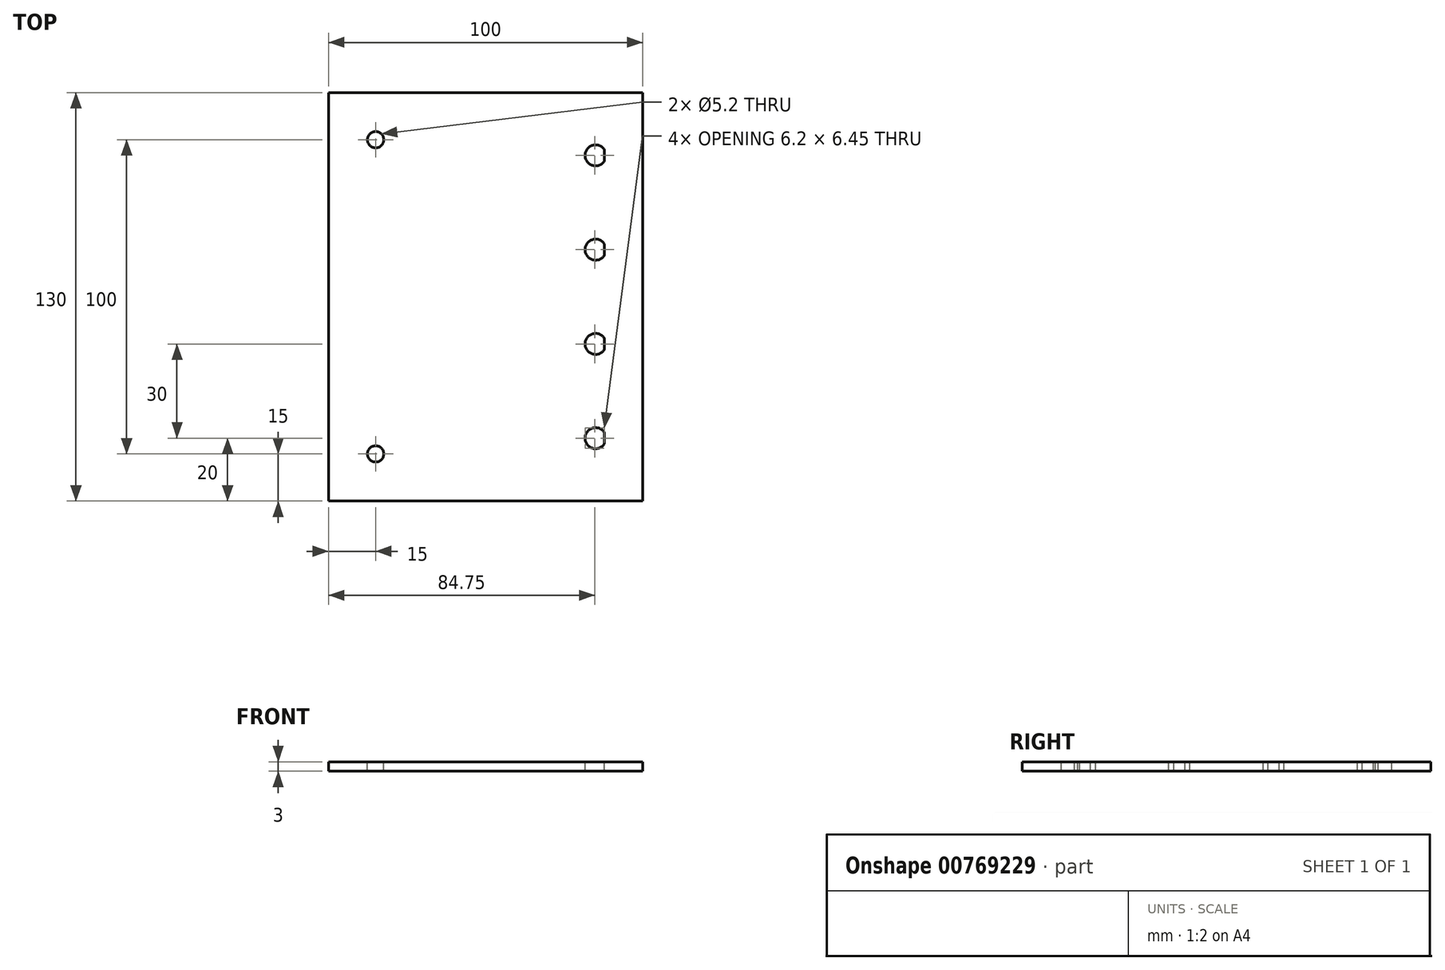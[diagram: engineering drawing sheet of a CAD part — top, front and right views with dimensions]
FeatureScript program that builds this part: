
annotation { "Feature Type Name" : "Feature", "Feature Type Description" : "" }
export const myFeature = defineFeature(function(context is Context, id is Id, definition is map)
    precondition{}
    {
        {
            var Q0;
            Q0=qCreatedBy(makeId("Top.planeOp"),FACE);
            var sketch = newSketch(context, id + "F0", { "sketchPlane" : qUnion([Q0])});
            skLineSegment(sketch, "E0.bottom", {"start": v(-56.25, -56.34) * mm, "end": v(43.75, -56.34) * mm});
            skLineSegment(sketch, "E0.top", {"start": v(-56.25, 73.66) * mm, "end": v(43.75, 73.66) * mm});
            skLineSegment(sketch, "E0.left", {"start": v(-56.25, -56.34) * mm, "end": v(-56.25, 73.66) * mm});
            skLineSegment(sketch, "E0.right", {"start": v(43.75, -56.34) * mm, "end": v(43.75, 73.66) * mm});
            skSolve(sketch);
        }
        {
            var Q0;
            Q0 = qSketchRegion(id + "F0", true);
            extrude(context, id + "F1", {"entities" : qUnion([Q0]), "depth" : 3 * mm, "offsetDistance" : 25 * mm});
        }
        {
            var Q0;
            Q0=makeQuery(id+"F1.opExtrude","CAP_FACE",FACE,{"disambiguationData":[OSD([sQuery(id+"F0.wireOp",EDGE,"E0.bottom"),sQuery(id+"F0.wireOp",EDGE,"E0.top"),sQuery(id+"F0.wireOp",EDGE,"E0.left"),sQuery(id+"F0.wireOp",EDGE,"E0.right")])],"isStart":false});
            var sketch = newSketch(context, id + "F2", { "sketchPlane" : qUnion([Q0])});
            skPoint(sketch, "E1", {"position": v(-41.25, -41.34) * mm});
            skPoint(sketch, "E2", {"position": v(-41.25, 58.66) * mm});
            skCircle(sketch, "E3", {"center": v(-41.25, -41.34) * mm, "radius": 2.6 * mm});
            skCircle(sketch, "E4", {"center": v(-41.25, 58.66) * mm, "radius": 2.6 * mm});
            skSolve(sketch);
        }
        {
            var Q0;
            Q0 = qSketchRegion(id + "F2", true);
            extrude(context, id + "F3", {"entities" : qUnion([Q0]), "operationType" : NewBodyOperationType.REMOVE, "endBound" : BoundingType.THROUGH_ALL, "oppositeDirection" : true, "depth" : 25 * mm, "offsetDistance" : 25 * mm});
        }
        {
            var Q0;
            Q0=makeQuery(id+"F1.opExtrude","CAP_FACE",FACE,{"disambiguationData":[OSD([sQuery(id+"F0.wireOp",EDGE,"E0.bottom"),sQuery(id+"F0.wireOp",EDGE,"E0.top"),sQuery(id+"F0.wireOp",EDGE,"E0.left"),sQuery(id+"F0.wireOp",EDGE,"E0.right")])],"isStart":false});
            var sketch = newSketch(context, id + "F4", { "sketchPlane" : qUnion([Q0])});
            skPoint(sketch, "E5", {"position": v(28.75, -36.34) * mm});
            skPoint(sketch, "E6", {"position": v(28.75, -6.34) * mm});
            skPoint(sketch, "E7", {"position": v(28.75, 23.66) * mm});
            skPoint(sketch, "E8", {"position": v(28.75, 53.66) * mm});
            skCircle(sketch, "E9", {"center": v(28.75, -36.34) * mm, "radius": 3.35 * mm});
            skCircle(sketch, "E10", {"center": v(28.75, -6.34) * mm, "radius": 3.35 * mm});
            skCircle(sketch, "E11", {"center": v(28.75, 23.66) * mm, "radius": 3.35 * mm});
            skCircle(sketch, "E12", {"center": v(28.75, 53.66) * mm, "radius": 3.35 * mm});
            skSolve(sketch);
        }
        {
            var Q0;
            Q0 = qSketchRegion(id + "F4", true);
            extrude(context, id + "F5", {"entities" : qUnion([Q0]), "operationType" : NewBodyOperationType.REMOVE, "endBound" : BoundingType.THROUGH_ALL, "oppositeDirection" : true, "depth" : 25 * mm, "offsetDistance" : 25 * mm});
        }
        {
            var Q0;
            Q0=makeQuery(id+"F1.opExtrude","SWEPT_FACE",FACE,{"disambiguationData":[OSD([sQuery(id+"F0.wireOp",EDGE,"E0.right")])]});
            var sketch = newSketch(context, id + "F6", { "sketchPlane" : qUnion([Q0])});
            skLineSegment(sketch, "E13.bottom", {"start": v(-56.34, 3) * mm, "end": v(73.66, 3) * mm});
            skLineSegment(sketch, "E13.top", {"start": v(-56.34, 0) * mm, "end": v(73.66, 0) * mm});
            skLineSegment(sketch, "E13.left", {"start": v(-56.34, 3) * mm, "end": v(-56.34, 0) * mm});
            skLineSegment(sketch, "E13.right", {"start": v(73.66, 3) * mm, "end": v(73.66, 0) * mm});
            skSolve(sketch);
        }
        {
            var Q0;
            Q0 = qSketchRegion(id + "F6", true);
            extrude(context, id + "F7", {"entities" : qUnion([Q0]), "operationType" : NewBodyOperationType.ADD, "oppositeDirection" : true, "depth" : 12.15 * mm, "offsetDistance" : 25 * mm});
        }
    });
